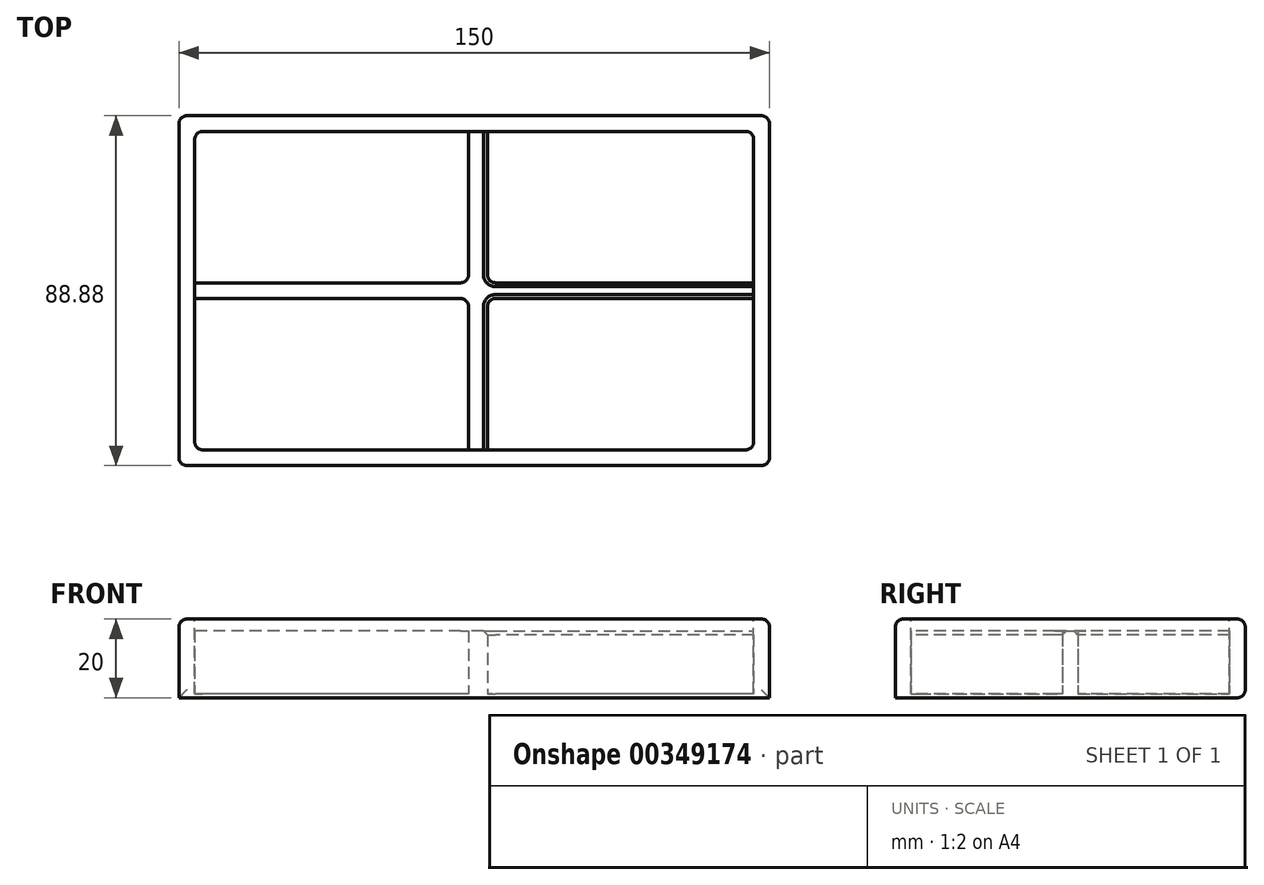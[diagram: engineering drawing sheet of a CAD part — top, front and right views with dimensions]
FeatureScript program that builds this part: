
annotation { "Feature Type Name" : "Feature", "Feature Type Description" : "" }
export const myFeature = defineFeature(function(context is Context, id is Id, definition is map)
    precondition{}
    {
        {
            var Q0;
            Q0=qCreatedBy(makeId("Top.planeOp"),FACE);
            var sketch = newSketch(context, id + "F0", { "sketchPlane" : qUnion([Q0])});
            skLineSegment(sketch, "E0.bottom", {"start": v(75, -44.44) * mm, "end": v(-75, -44.44) * mm});
            skLineSegment(sketch, "E0.top", {"start": v(75, 44.44) * mm, "end": v(-75, 44.44) * mm});
            skLineSegment(sketch, "E0.left", {"start": v(75, -44.44) * mm, "end": v(75, 44.44) * mm});
            skLineSegment(sketch, "E0.right", {"start": v(-75, -44.44) * mm, "end": v(-75, 44.44) * mm});
            skPoint(sketch, "E0.middle", {"position": v(0, 0) * mm});
            skSolve(sketch);
        }
        {
            var Q0;
            Q0 = qSketchRegion(id + "F0", true);
            extrude(context, id + "F1", {"entities" : qUnion([Q0]), "depth" : 20 * mm});
        }
        {
            var Q0;
            Q0=makeQuery(id+"F1.opExtrude","CAP_FACE",FACE,{"disambiguationData":[OSD([sQuery(id+"F0.wireOp",EDGE,"E0.bottom"),sQuery(id+"F0.wireOp",EDGE,"E0.top"),sQuery(id+"F0.wireOp",EDGE,"E0.left"),sQuery(id+"F0.wireOp",EDGE,"E0.right")])],"isStart":false});
            var sketch = newSketch(context, id + "F2", { "sketchPlane" : qUnion([Q0])});
            skLineSegment(sketch, "E1.bottom", {"start": v(71, -40.44) * mm, "end": v(-71, -40.44) * mm});
            skLineSegment(sketch, "E1.top", {"start": v(71, 40.44) * mm, "end": v(-71, 40.44) * mm});
            skLineSegment(sketch, "E1.left", {"start": v(71, -40.44) * mm, "end": v(71, 40.44) * mm});
            skLineSegment(sketch, "E1.right", {"start": v(-71, -40.44) * mm, "end": v(-71, 40.44) * mm});
            skPoint(sketch, "E1.middle", {"position": v(0, 0) * mm});
            skSolve(sketch);
        }
        {
            var Q0;
            Q0 = qSketchRegion(id + "F2", true);
            extrude(context, id + "F3", {"entities" : qUnion([Q0]), "operationType" : NewBodyOperationType.REMOVE, "oppositeDirection" : true, "depth" : 19 * mm});
        }
        {
            var Q0;
            Q0=makeQuery(id+"F3.boolean.opBoolean","COPY",FACE,{"derivedFrom":makeQuery(id+"F3.opExtrude","CAP_FACE",FACE,{"disambiguationData":[OSD([sQuery(id+"F2.wireOp",EDGE,"E1.bottom"),sQuery(id+"F2.wireOp",EDGE,"E1.top"),sQuery(id+"F2.wireOp",EDGE,"E1.left"),sQuery(id+"F2.wireOp",EDGE,"E1.right")])],"isStart":false})});
            var sketch = newSketch(context, id + "F4", { "sketchPlane" : qUnion([Q0])});
            skLineSegment(sketch, "E2.bottom", {"start": v(71, -2) * mm, "end": v(3.37, -2) * mm});
            skLineSegment(sketch, "E2.top", {"start": v(71, 2) * mm, "end": v(3.37, 2) * mm});
            skLineSegment(sketch, "E2.left", {"start": v(71, -2) * mm, "end": v(71, 2) * mm});
            skLineSegment(sketch, "E2.right", {"start": v(-71, -2) * mm, "end": v(-71, 2) * mm});
            skPoint(sketch, "E2.middle", {"position": v(0, 0) * mm});
            skPoint(sketch, "E3.middle", {"position": v(0, 42.54) * mm});
            skLineSegment(sketch, "E4.trimOffspring", {"start": v(-1.43, -2) * mm, "end": v(-71, -2) * mm});
            skLineSegment(sketch, "E5.trimOffspring", {"start": v(-1.43, 2) * mm, "end": v(-71, 2) * mm});
            skLineSegment(sketch, "E6.bottom", {"start": v(-1.43, 40.44) * mm, "end": v(3.37, 40.44) * mm});
            skLineSegment(sketch, "E6.top", {"start": v(-1.43, -40.44) * mm, "end": v(3.37, -40.44) * mm});
            skLineSegment(sketch, "E6.left", {"start": v(-1.43, 40.44) * mm, "end": v(-1.43, 2) * mm});
            skLineSegment(sketch, "E6.right", {"start": v(3.37, 40.44) * mm, "end": v(3.37, 2) * mm});
            skPoint(sketch, "E7.orphan", {"position": v(0, 2) * mm});
            skPoint(sketch, "E8.orphan", {"position": v(0, -2) * mm});
            skLineSegment(sketch, "E9.trimOffspring", {"start": v(-1.43, -2) * mm, "end": v(-1.43, -40.44) * mm});
            skLineSegment(sketch, "E10.trimOffspring", {"start": v(3.37, -2) * mm, "end": v(3.37, -40.44) * mm});
            skSolve(sketch);
        }
        {
            var Q0;
            Q0 = qSketchRegion(id + "F4", true);
            extrude(context, id + "F5", {"entities" : qUnion([Q0]), "operationType" : NewBodyOperationType.ADD, "depth" : 16 * mm});
        }
        {
            var Q0;
            Q0=makeQuery(id+"F1.opExtrude","CAP_EDGE",EDGE,{"disambiguationData":[OSD([sQuery(id+"F0.wireOp",EDGE,"E0.right")])],"isStart":false});
            var Q1;
            Q1=makeQuery(id+"F1.opExtrude","CAP_EDGE",EDGE,{"disambiguationData":[OSD([sQuery(id+"F0.wireOp",EDGE,"E0.top")])],"isStart":false});
            var Q2;
            Q2=makeQuery(id+"F1.opExtrude","CAP_EDGE",EDGE,{"disambiguationData":[OSD([sQuery(id+"F0.wireOp",EDGE,"E0.bottom")])],"isStart":false});
            var Q3;
            Q3=makeQuery(id+"F1.opExtrude","CAP_EDGE",EDGE,{"disambiguationData":[OSD([sQuery(id+"F0.wireOp",EDGE,"E0.left")])],"isStart":false});
            var Q4;
            Q4=makeQuery(id+"F1.opExtrude","SWEPT_EDGE",EDGE,{"disambiguationData":[OSD([sQuery(id+"F0.wireOp",EDGE,"E0.bottom"),sQuery(id+"F0.wireOp",EDGE,"E0.right")])]});
            var Q5;
            Q5=makeQuery(id+"F1.opExtrude","SWEPT_EDGE",EDGE,{"disambiguationData":[OSD([sQuery(id+"F0.wireOp",EDGE,"E0.top"),sQuery(id+"F0.wireOp",EDGE,"E0.right")])]});
            var Q6;
            Q6=makeQuery(id+"F1.opExtrude","SWEPT_EDGE",EDGE,{"disambiguationData":[OSD([sQuery(id+"F0.wireOp",EDGE,"E0.bottom"),sQuery(id+"F0.wireOp",EDGE,"E0.left")])]});
            var Q7;
            Q7=makeQuery(id+"F1.opExtrude","SWEPT_FACE",FACE,{"disambiguationData":[OSD([sQuery(id+"F0.wireOp",EDGE,"E0.top")])]});
            var Q8;
            Q8=makeQuery(id+"F3.boolean.opBoolean","COPY",EDGE,{"derivedFrom":makeQuery(id+"F3.opExtrude","SWEPT_EDGE",EDGE,{"disambiguationData":[OSD([sQuery(id+"F2.wireOp",EDGE,"E1.bottom"),sQuery(id+"F2.wireOp",EDGE,"E1.right")])]})});
            var Q9;
            Q9=makeQuery(id+"F3.boolean.opBoolean","COPY",EDGE,{"derivedFrom":makeQuery(id+"F3.opExtrude","SWEPT_EDGE",EDGE,{"disambiguationData":[OSD([sQuery(id+"F2.wireOp",EDGE,"E1.top"),sQuery(id+"F2.wireOp",EDGE,"E1.right")])]})});
            var Q10;
            Q10=makeQuery(id+"F3.boolean.opBoolean","COPY",EDGE,{"derivedFrom":makeQuery(id+"F3.opExtrude","SWEPT_EDGE",EDGE,{"disambiguationData":[OSD([sQuery(id+"F2.wireOp",EDGE,"E1.bottom"),sQuery(id+"F2.wireOp",EDGE,"E1.left")])]})});
            var Q11;
            Q11=makeQuery(id+"F3.boolean.opBoolean","COPY",EDGE,{"derivedFrom":makeQuery(id+"F3.opExtrude","SWEPT_EDGE",EDGE,{"disambiguationData":[OSD([sQuery(id+"F2.wireOp",EDGE,"E1.top"),sQuery(id+"F2.wireOp",EDGE,"E1.left")])]})});
            var Q12;
            Q12=makeQuery(id+"F5.opExtrude","SWEPT_EDGE",EDGE,{"disambiguationData":[OSD([sQuery(id+"F2.wireOp",EDGE,"E1.left"),sQuery(id+"F4.wireOp",EDGE,"E2.top"),sQuery(id+"F4.wireOp",EDGE,"E2.left")])]});
            var Q13;
            Q13=makeQuery(id+"F5.opExtrude","SWEPT_EDGE",EDGE,{"disambiguationData":[OSD([sQuery(id+"F2.wireOp",EDGE,"E1.bottom"),sQuery(id+"F4.wireOp",EDGE,"qdZOQg0f-a6iM-vjKW-caG4-i3gp1lJXyZht.top"),sQuery(id+"F4.wireOp",EDGE,"qdZOQg0f-a6iM-vjKW-caG4-i3gp1lJXyZht.left")])]});
            var Q14;
            Q14=makeQuery(id+"F5.opExtrude","SWEPT_EDGE",EDGE,{"disambiguationData":[OSD([sQuery(id+"F2.wireOp",EDGE,"E1.left"),sQuery(id+"F4.wireOp",EDGE,"E2.bottom"),sQuery(id+"F4.wireOp",EDGE,"E2.left")])]});
            var Q15;
            Q15=makeQuery(id+"F5.opExtrude","SWEPT_EDGE",EDGE,{"disambiguationData":[OSD([sQuery(id+"F4.wireOp",EDGE,"E2.bottom"),sQuery(id+"F4.wireOp",EDGE,"qdZOQg0f-a6iM-vjKW-caG4-i3gp1lJXyZht.bottom"),sQuery(id+"F4.wireOp",EDGE,"qdZOQg0f-a6iM-vjKW-caG4-i3gp1lJXyZht.left")])]});
            var Q16;
            Q16=makeQuery(id+"F5.opExtrude","SWEPT_EDGE",EDGE,{"disambiguationData":[OSD([sQuery(id+"F2.wireOp",EDGE,"E1.bottom"),sQuery(id+"F4.wireOp",EDGE,"qdZOQg0f-a6iM-vjKW-caG4-i3gp1lJXyZht.top"),sQuery(id+"F4.wireOp",EDGE,"qdZOQg0f-a6iM-vjKW-caG4-i3gp1lJXyZht.right")])]});
            var Q17;
            Q17=makeQuery(id+"F5.opExtrude","SWEPT_EDGE",EDGE,{"disambiguationData":[OSD([sQuery(id+"F2.wireOp",EDGE,"E1.right"),sQuery(id+"F4.wireOp",EDGE,"E2.top"),sQuery(id+"F4.wireOp",EDGE,"E2.right")])]});
            var Q18;
            Q18=makeQuery(id+"F5.opExtrude","SWEPT_EDGE",EDGE,{"disambiguationData":[OSD([sQuery(id+"F2.wireOp",EDGE,"E1.right"),sQuery(id+"F4.wireOp",EDGE,"E2.bottom"),sQuery(id+"F4.wireOp",EDGE,"E2.right")])]});
            var Q19;
            Q19=makeQuery(id+"F3.boolean.opBoolean","COPY",EDGE,{"derivedFrom":makeQuery(id+"F3.opExtrude","CAP_EDGE",EDGE,{"disambiguationData":[OSD([sQuery(id+"F2.wireOp",EDGE,"E1.left")])],"isStart":true})});
            var Q20;
            Q20=makeQuery(id+"F3.boolean.opBoolean","COPY",EDGE,{"derivedFrom":makeQuery(id+"F3.opExtrude","CAP_EDGE",EDGE,{"disambiguationData":[OSD([sQuery(id+"F2.wireOp",EDGE,"E1.top")])],"isStart":true})});
            var Q21;
            Q21=makeQuery(id+"F3.boolean.opBoolean","COPY",EDGE,{"derivedFrom":makeQuery(id+"F3.opExtrude","CAP_EDGE",EDGE,{"disambiguationData":[OSD([sQuery(id+"F2.wireOp",EDGE,"E1.bottom")])],"isStart":true})});
            var Q22;
            Q22=makeQuery(id+"F3.boolean.opBoolean","COPY",EDGE,{"derivedFrom":makeQuery(id+"F3.opExtrude","CAP_EDGE",EDGE,{"disambiguationData":[OSD([sQuery(id+"F2.wireOp",EDGE,"E1.right")])],"isStart":true})});
            var Q23;
            Q23=makeQuery(id+"F5.opExtrude","SWEPT_EDGE",EDGE,{"disambiguationData":[OSD([sQuery(id+"F4.wireOp",EDGE,"E2.bottom"),sQuery(id+"F4.wireOp",EDGE,"qdZOQg0f-a6iM-vjKW-caG4-i3gp1lJXyZht.bottom"),sQuery(id+"F4.wireOp",EDGE,"qdZOQg0f-a6iM-vjKW-caG4-i3gp1lJXyZht.right")])]});
            var Q24;
            Q24=makeQuery(id+"F5.opExtrude","SWEPT_EDGE",EDGE,{"disambiguationData":[OSD([sQuery(id+"F4.wireOp",EDGE,"E5.trimOffspring"),sQuery(id+"F4.wireOp",EDGE,"E6.left")])]});
            var Q25;
            Q25=makeQuery(id+"F5.opExtrude","SWEPT_EDGE",EDGE,{"disambiguationData":[OSD([sQuery(id+"F4.wireOp",EDGE,"E2.top"),sQuery(id+"F4.wireOp",EDGE,"E6.right")])]});
            var Q26;
            Q26=makeQuery(id+"F5.opExtrude","SWEPT_EDGE",EDGE,{"disambiguationData":[OSD([sQuery(id+"F4.wireOp",EDGE,"E4.trimOffspring"),sQuery(id+"F4.wireOp",EDGE,"E9.trimOffspring")])]});
            var Q27;
            Q27=makeQuery(id+"F5.opExtrude","SWEPT_EDGE",EDGE,{"disambiguationData":[OSD([sQuery(id+"F2.wireOp",EDGE,"E1.top"),sQuery(id+"F4.wireOp",EDGE,"E6.bottom"),sQuery(id+"F4.wireOp",EDGE,"E6.left")])]});
            var Q28;
            Q28=makeQuery(id+"F5.opExtrude","SWEPT_EDGE",EDGE,{"disambiguationData":[OSD([sQuery(id+"F2.wireOp",EDGE,"E1.top"),sQuery(id+"F4.wireOp",EDGE,"E6.bottom"),sQuery(id+"F4.wireOp",EDGE,"E6.right")])]});
            fillet(context, id + "F6", {"entities" : qUnion([Q0, Q1, Q2, Q3, Q4, Q5, Q6, Q7, Q8, Q9, Q10, Q11, Q12, Q13, Q14, Q15, Q16, Q17, Q18, Q19, Q20, Q21, Q22, Q23, Q24, Q25, Q26, Q27, Q28]), "radius" : 2 * mm, "tangentPropagation" : true, "allowEdgeOverflow" : false});
        }
        {
            var Q0;
            Q0=makeQuery(id+"F5.opExtrude","CAP_EDGE",EDGE,{"disambiguationData":[OSD([sQuery(id+"F4.wireOp",EDGE,"E2.top")])],"isStart":false});
            var Q1;
            {var subQ0=sQuery(id+"F4.wireOp",EDGE,"E2.bottom");Q1=makeQuery(id+"F5.opExtrude","CAP_EDGE",EDGE,{"disambiguationData":[OSD([subQ0]),TDD([makeQuery(id+"F4.imprint","IMPRINT",EDGE,{"disambiguationData":[TD([[makeQuery(id+"F4.imprint","INTERSECT",VERTEX,{"derivedFrom":[makeQuery(id+"F3.boolean.opBoolean","COPY",EDGE,{"derivedFrom":makeQuery(id+"F3.opExtrude","CAP_EDGE",EDGE,{"disambiguationData":[OSD([sQuery(id+"F2.wireOp",EDGE,"E1.left")])],"isStart":false})}),subQ0,sQuery(id+"F4.wireOp",EDGE,"E2.left")]}),-1.0]])],"derivedFrom":subQ0})])],"isStart":false});}
            var Q2;
            {var subQ0=sQuery(id+"F4.wireOp",EDGE,"E2.bottom");Q2=makeQuery(id+"F5.opExtrude","CAP_EDGE",EDGE,{"disambiguationData":[OSD([subQ0]),TDD([makeQuery(id+"F4.imprint","IMPRINT",EDGE,{"disambiguationData":[TD([[makeQuery(id+"F4.imprint","INTERSECT",VERTEX,{"derivedFrom":[makeQuery(id+"F3.boolean.opBoolean","COPY",EDGE,{"derivedFrom":makeQuery(id+"F3.opExtrude","CAP_EDGE",EDGE,{"disambiguationData":[OSD([sQuery(id+"F2.wireOp",EDGE,"E1.right")])],"isStart":false})}),subQ0,sQuery(id+"F4.wireOp",EDGE,"E2.right")]}),1.0]])],"derivedFrom":subQ0})])],"isStart":false});}
            var Q3;
            Q3=makeQuery(id+"F5.opExtrude","CAP_EDGE",EDGE,{"disambiguationData":[OSD([sQuery(id+"F4.wireOp",EDGE,"qdZOQg0f-a6iM-vjKW-caG4-i3gp1lJXyZht.right")])],"isStart":false});
            var Q4;
            Q4=makeQuery(id+"F5.opExtrude","CAP_EDGE",EDGE,{"disambiguationData":[OSD([sQuery(id+"F4.wireOp",EDGE,"qdZOQg0f-a6iM-vjKW-caG4-i3gp1lJXyZht.left")])],"isStart":false});
            chamfer(context, id + "F7", {"entities" : qUnion([Q0, Q1, Q2, Q3, Q4]), "width" : 1 * mm, "tangentPropagation" : true});
        }
    });
